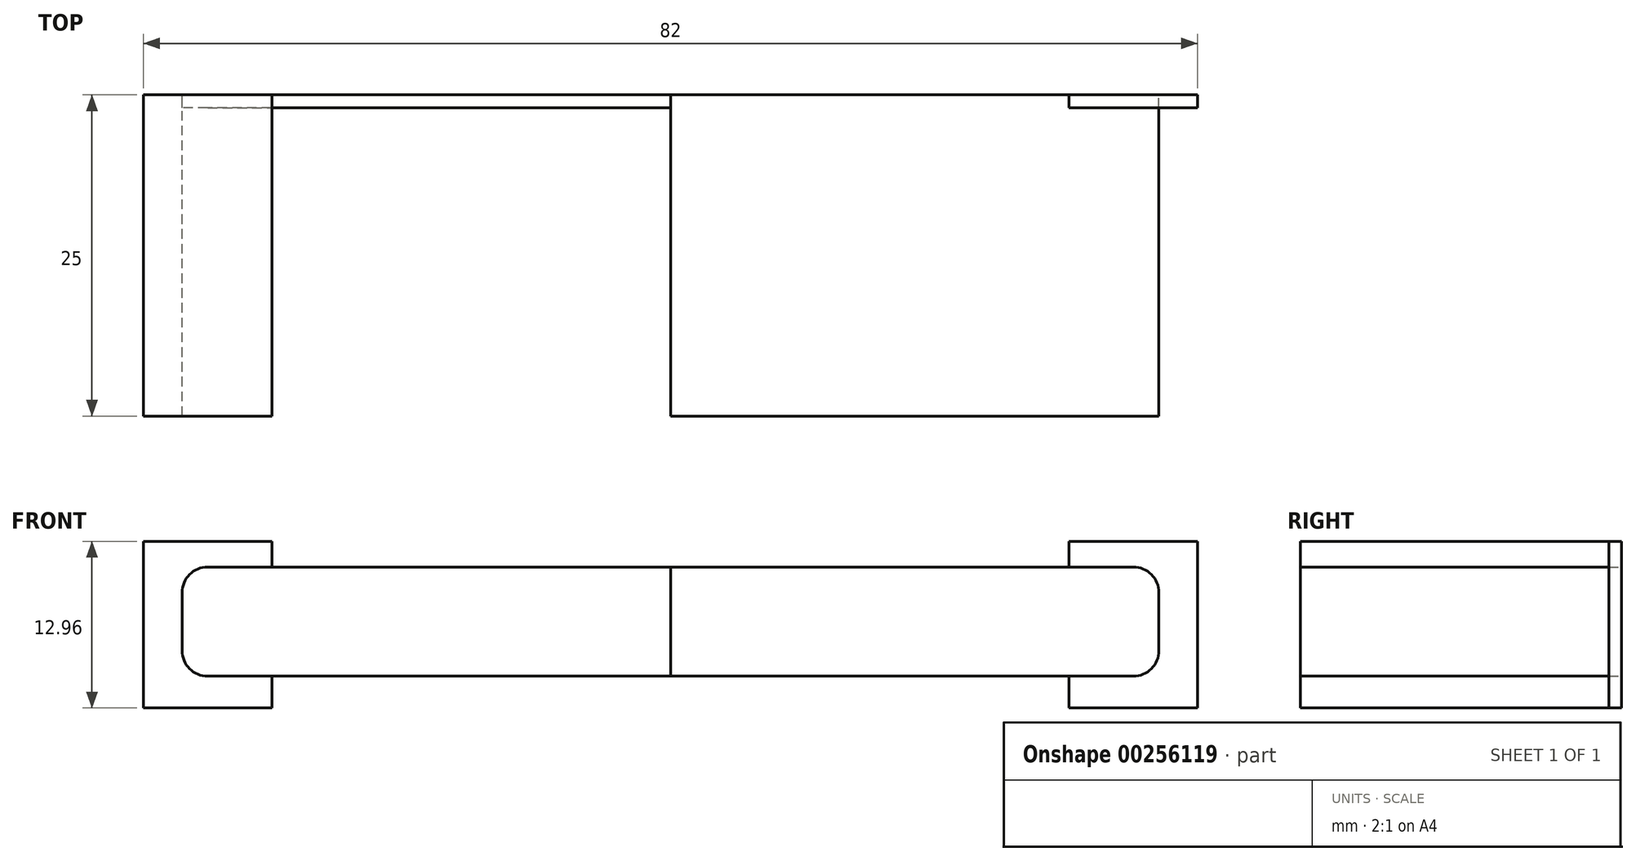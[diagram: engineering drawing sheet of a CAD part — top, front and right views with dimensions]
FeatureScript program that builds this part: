
annotation { "Feature Type Name" : "Feature", "Feature Type Description" : "" }
export const myFeature = defineFeature(function(context is Context, id is Id, definition is map)
    precondition{}
    {
        {
            var Q0;
            Q0=qCreatedBy(makeId("Front.planeOp"),FACE);
            var sketch = newSketch(context, id + "F0", { "sketchPlane" : qUnion([Q0])});
            skLineSegment(sketch, "E0", {"start": v(-38, 0) * mm, "end": v(-74, 0) * mm});
            skLineSegment(sketch, "E1", {"start": v(-76, 2) * mm, "end": v(-76, 6.5) * mm});
            skLineSegment(sketch, "E2", {"start": v(-74, 8.5) * mm, "end": v(-38, 8.5) * mm});
            skPoint(sketch, "E3.visualSharp", {"position": v(-76, 0) * mm});
            skArc(sketch, "E3.filletArc", {"start": v(-76, 2) * mm, "mid": v(-75.41, 0.59) * mm, "end": v(-74, 0) * mm});
            skPoint(sketch, "E4.visualSharp", {"position": v(-76, 8.5) * mm});
            skArc(sketch, "E4.filletArc", {"start": v(-74, 8.5) * mm, "mid": v(-75.41, 7.91) * mm, "end": v(-76, 6.5) * mm});
            skPoint(sketch, "E5.visualSharp", {"position": v(0, 8.5) * mm});
            skPoint(sketch, "E6.visualSharp", {"position": v(0, 0) * mm});
            skLineSegment(sketch, "E7", {"start": v(-74, 8.5) * mm, "end": v(-69, 8.5) * mm, "construction": true});
            skLineSegment(sketch, "E8", {"start": v(-69, 8.5) * mm, "end": v(-69, 10.5) * mm});
            skLineSegment(sketch, "E9", {"start": v(-69, 10.5) * mm, "end": v(-79, 10.5) * mm});
            skLineSegment(sketch, "E10", {"start": v(-79, 10.5) * mm, "end": v(-79, -2.46) * mm});
            skLineSegment(sketch, "E11", {"start": v(-79, -2.46) * mm, "end": v(-69, -2.46) * mm});
            skLineSegment(sketch, "E12", {"start": v(-69, -2.46) * mm, "end": v(-69, 0) * mm});
            skLineSegment(sketch, "E13", {"start": v(-38, -4.65) * mm, "end": v(-38, 16.41) * mm});
            skArc(sketch, "E14.MirrorCS", {"start": v(-2, 8.5) * mm, "mid": v(-0.59, 7.91) * mm, "end": v(0, 6.5) * mm});
            skArc(sketch, "E15.MirrorCS", {"start": v(0, 2) * mm, "mid": v(-0.59, 0.59) * mm, "end": v(-2, 0) * mm});
            skLineSegment(sketch, "E16.MirrorCS", {"start": v(3, -2.46) * mm, "end": v(-7, -2.46) * mm});
            skLineSegment(sketch, "E17.MirrorCS", {"start": v(3, 10.5) * mm, "end": v(3, -2.46) * mm});
            skLineSegment(sketch, "E18.MirrorCS", {"start": v(-7, 10.5) * mm, "end": v(3, 10.5) * mm});
            skLineSegment(sketch, "E19.MirrorCS", {"start": v(-7, 8.5) * mm, "end": v(-7, 10.5) * mm});
            skLineSegment(sketch, "E20.MirrorCS", {"start": v(-2, 8.5) * mm, "end": v(-7, 8.5) * mm, "construction": true});
            skLineSegment(sketch, "E21.MirrorCS", {"start": v(-7, -2.46) * mm, "end": v(-7, 0) * mm});
            skLineSegment(sketch, "E22.MirrorCS", {"start": v(0, 2) * mm, "end": v(0, 6.5) * mm});
            skLineSegment(sketch, "E23.MirrorCS", {"start": v(-2, 8.5) * mm, "end": v(-38, 8.5) * mm});
            skLineSegment(sketch, "E24.MirrorCS", {"start": v(-38, 0) * mm, "end": v(-2, 0) * mm});
            skSolve(sketch);
        }
        {
            var Q0;
            Q0=makeQuery(id+"F0.imprint","IMPRINT",FACE,{"disambiguationData":[TD([[makeQuery(id+"F0.imprint","IMPRINT",EDGE,{"derivedFrom":sQuery(id+"F0.wireOp",EDGE,"E1")}),1.0]])]});
            var Q1;
            {var subQ2=sQuery(id+"F0.wireOp",EDGE,"E14.MirrorCS");Q1=makeQuery(id+"F0.imprint","IMPRINT",FACE,{"disambiguationData":[TD([[makeQuery(id+"F0.imprint","IMPRINT",EDGE,{"derivedFrom":subQ2}),1.0]])]});}
            extrude(context, id + "F1", {"entities" : qUnion([Q0, Q1]), "depth" : 25 * mm});
        }
        {
            var Q0;
            Q0=makeQuery(id+"F0.imprint","IMPRINT",FACE,{"disambiguationData":[TD([[makeQuery(id+"F0.imprint","IMPRINT",EDGE,{"derivedFrom":sQuery(id+"F0.wireOp",EDGE,"E1")}),-1.0]])]});
            var Q1;
            {var subQ1=sQuery(id+"F0.wireOp",EDGE,"E14.MirrorCS");Q1=makeQuery(id+"F0.imprint","IMPRINT",FACE,{"disambiguationData":[TD([[makeQuery(id+"F0.imprint","IMPRINT",EDGE,{"derivedFrom":subQ1}),-1.0]])]});}
            extrude(context, id + "F2", {"entities" : qUnion([Q0, Q1]), "depth" : 1 * mm});
        }
    });
